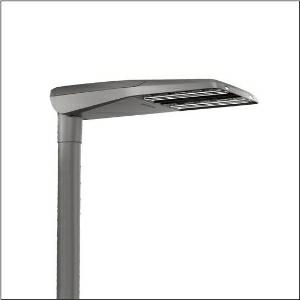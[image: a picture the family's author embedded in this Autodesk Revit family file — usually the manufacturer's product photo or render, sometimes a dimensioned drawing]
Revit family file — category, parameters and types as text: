
# Revit family: streetlight_sl_11_iq_midi___st1_0p1_0_5xc3k51g08me_2a46
name_source: partatom
category: Lighting Fixtures
units: mm (PartAtom-declared; Revit-internal decimal feet)

## family parameters
Cut with Voids When Loaded = No
Host = Face
Light Source = No
Part Type = Normal
Room Calculation Point = No
Round Connector Dimension = Use Diameter
Shared = No

## types (1)
- --- (1 x LED, 17540 lm, 122.7 W, 3000K)
    Apparent Load = 123 VA
    CIE Flux Codes = 32 65 95 100 100
    Color Rendering = 70
    Color Temperature = 3000K
    Default Elevation = 1800 mm
    Description = Streetlight SL 11 iQ midi, mast luminaire, primary light control with 3 zone facetted reflector, of plastic, silver coated, highly specular, primary optical cover: cover, of PMMA, transparent, light distribution: ST1.0P1.0, light emission: direct distribution, primary light characteristic: asymmetric, installation type: post-top, side-entry, lamps: LED, High Power LED, rated values: 17.540lm | 122,7W | 143lm/W (begin service life); end service life: 17.540lm | 130,2W; at 50% lumin. flux: 8.770lm | 56,1W | 156,3lm/W, colour temperature: 3000K, colour rendering: CRI > 70, light colour: 730, light setting 1 begin service life: 100% | 17.540lm | 122,7W | 143lm/W | 3.000K, light setting 1 end service life: 130,2W, further light settings possible, control: Street-Remote, Auto-Match, Temp-Guard, Lumen-Switch, Night-Set, Smart-Wire, Light-Fading, Desk-Remote (wireless, voltage-free reading and setting of iQ features in the workshop via application-optimized NFC function/RFID function), optimised constant luminous flux control (CLO 2.0), pre-setting: linear dimming characteristic, with cable H07RN-F 5x 1.5mm², mains connection: 230..240V, AC, 50/60Hz, connection cable pre-assembled, cable length: 12,5m, luminaire housing, of diecast aluminium, powder-coated, SITECO metallic grey (DB 702S), please order mast flange separately, inclination adjustable without tools: 0°, 5°, 10°, 15° (post-top) | 0°, -5°, -10°, -15° (side-entry), sealing non-destructively replaceable, multi-level sealing system, length: 780mm, width: 376mm, height: 118mm, mast flange for spigot size: 42mm (side-entry): 5XC10008XM4, 60/48mm (side-entry/post-top): 5XC10108XM2, 76/60mm (side-entry/post-top): 5XC10108XM1, equipment: Power, protection rating (complete): IP66, insulation class (complete): insulation class II (safety insulation), certification: CE, ENEC, ENEC+, VDE, impact resistance: IK10, permissible operating ambient temperature for outdoor applications: -25..+50°C, standard-compliant lighting for roads and squares, Environmental Product Declaration (EPD) tested and certified by an independent institute, packaging unit: 1 piece

Light Distribution: ST1.0P1.0
    Height = 118 mm
    Lamp = 1 x LED
    Lamp Light Flux = 17540 lm
    Lamp Power = 122.7 W
    Lamp count = 1
    Length = 780 mm
    Luminous efficacy = 143 lm/W
    Manufacturer = Siteco
    ModVariant = No
    Model = 5XC3K51G08ME
    Number of Poles = 1
    OnlyDefault = Yes
    Power Factor = 1
    Product Name = Streetlight SL 11 iQ midi | ST1.0P1.0
    Product group = mast luminaire | pylon top
    ProductGroupID = 6100
    Protection Class = Protection class II
    Protection Degree = IP 66
    RLX_Detail_Level = 1
    RLX_Emergency_Light_Flux = 0 lm
    RLX_Emergency_Type = 0
    RLX_Emergency_Type_DB = No
    RlxData = <blob elided: 71041 chars, md5=a0ad7dba>
    Socket = socket
    Standby Power = 0 W
    System Light Flux = 17540 lm
    System Power = 123 W
    Type Comments = factory setting: luminous flux: 100 % | dim-lin: 254 | 553 mA
    Type Image = l_1005960.jpg
    URL = http://relux.com
    VarID = @adj_027619
    Voltage = 0 V
    Weight = 0.00 kg
    Width = 376 mm

## geometry (parser evidence)
native form markers: Blend x4, Sweep x10
no freeform markers — native parametric forms only
